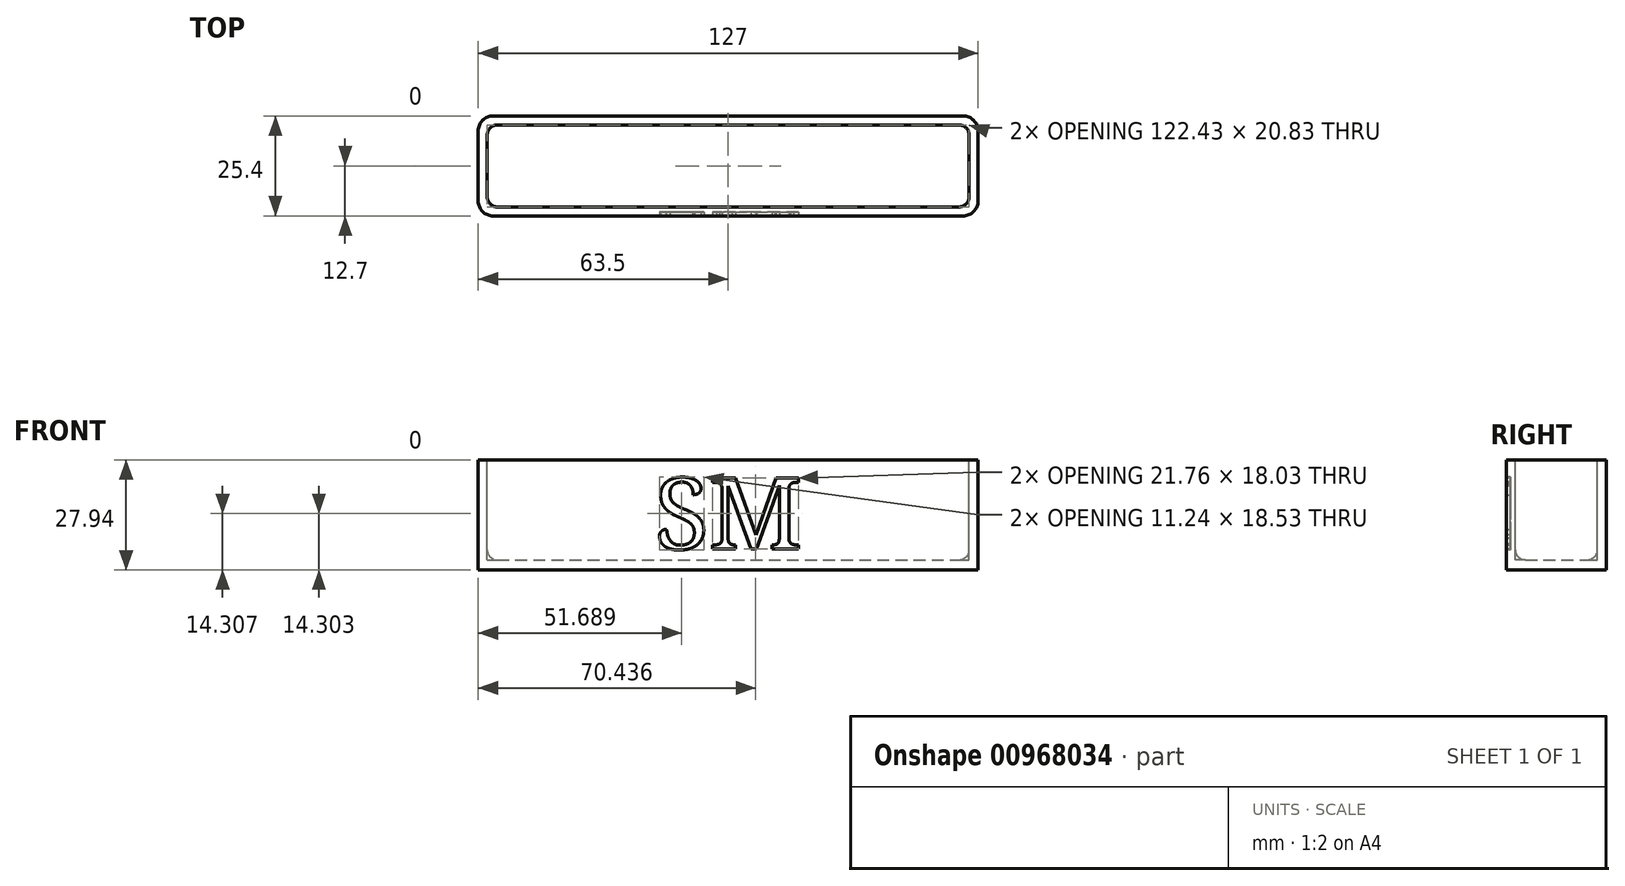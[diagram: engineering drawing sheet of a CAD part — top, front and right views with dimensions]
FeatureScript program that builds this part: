
annotation { "Feature Type Name" : "Feature", "Feature Type Description" : "" }
export const myFeature = defineFeature(function(context is Context, id is Id, definition is map)
    precondition{}
    {
        {
            var Q0;
            Q0=qCreatedBy(makeId("Top.planeOp"),FACE);
            var sketch = newSketch(context, id + "F0", { "sketchPlane" : qUnion([Q0])});
            skLineSegment(sketch, "E0.bottom", {"start": v(63.5, -12.7) * mm, "end": v(-63.5, -12.7) * mm});
            skLineSegment(sketch, "E0.top", {"start": v(63.5, 12.7) * mm, "end": v(-63.5, 12.7) * mm});
            skLineSegment(sketch, "E0.left", {"start": v(63.5, -12.7) * mm, "end": v(63.5, 12.7) * mm});
            skLineSegment(sketch, "E0.right", {"start": v(-63.5, -12.7) * mm, "end": v(-63.5, 12.7) * mm});
            skPoint(sketch, "E0.middle", {"position": v(0, 0) * mm});
            skSolve(sketch);
        }
        {
            var Q0;
            Q0=makeQuery(id+"F0.imprint","IMPRINT",FACE,{"disambiguationData":[TD([[makeQuery(id+"F0.imprint","IMPRINT",EDGE,{"derivedFrom":sQuery(id+"F0.wireOp",EDGE,"E0.bottom")}),-1.0]])]});
            extrude(context, id + "F1", {"entities" : qUnion([Q0]), "depth" : 27.94 * mm, "offsetDistance" : 25.4 * mm});
        }
        {
            var Q0;
            Q0=makeQuery(id+"F1.opExtrude","CAP_FACE",FACE,{"disambiguationData":[OSD([sQuery(id+"F0.wireOp",EDGE,"E0.bottom"),sQuery(id+"F0.wireOp",EDGE,"E0.top"),sQuery(id+"F0.wireOp",EDGE,"E0.left"),sQuery(id+"F0.wireOp",EDGE,"E0.right")])],"isStart":false});
            var sketch = newSketch(context, id + "F2", { "sketchPlane" : qUnion([Q0])});
            skLineSegment(sketch, "E1.0", {"start": v(61.21, -10.41) * mm, "end": v(61.21, 10.41) * mm});
            skLineSegment(sketch, "E1.1", {"start": v(-61.21, -10.41) * mm, "end": v(61.21, -10.41) * mm});
            skLineSegment(sketch, "E1.2", {"start": v(-61.21, 10.41) * mm, "end": v(-61.21, -10.41) * mm});
            skLineSegment(sketch, "E1.3", {"start": v(61.21, 10.41) * mm, "end": v(-61.21, 10.41) * mm});
            skSolve(sketch);
        }
        {
            var Q0;
            Q0=makeQuery(id+"F2.imprint","IMPRINT",FACE,{"disambiguationData":[TD([[makeQuery(id+"F2.imprint","IMPRINT",EDGE,{"derivedFrom":sQuery(id+"F2.wireOp",EDGE,"E1.0")}),1.0]])]});
            extrude(context, id + "F3", {"entities" : qUnion([Q0]), "operationType" : NewBodyOperationType.REMOVE, "oppositeDirection" : true, "depth" : 25.4 * mm, "offsetDistance" : 25.4 * mm});
        }
        {
            var Q0;
            Q0=makeQuery(id+"F3.boolean.opBoolean","COPY",FACE,{"derivedFrom":makeQuery(id+"F3.opExtrude","CAP_FACE",FACE,{"disambiguationData":[OSD([sQuery(id+"F2.wireOp",EDGE,"E1.0"),sQuery(id+"F2.wireOp",EDGE,"E1.1"),sQuery(id+"F2.wireOp",EDGE,"E1.2"),sQuery(id+"F2.wireOp",EDGE,"E1.3")])],"isStart":false})});
            var Q1;
            Q1=makeQuery(id+"F3.boolean.opBoolean","COPY",EDGE,{"derivedFrom":makeQuery(id+"F3.opExtrude","SWEPT_EDGE",EDGE,{"disambiguationData":[OSD([sQuery(id+"F2.wireOp",EDGE,"E1.2"),sQuery(id+"F2.wireOp",EDGE,"E1.3")])]})});
            var Q2;
            Q2=makeQuery(id+"F3.boolean.opBoolean","COPY",EDGE,{"derivedFrom":makeQuery(id+"F3.opExtrude","SWEPT_EDGE",EDGE,{"disambiguationData":[OSD([sQuery(id+"F2.wireOp",EDGE,"E1.0"),sQuery(id+"F2.wireOp",EDGE,"E1.3")])]})});
            var Q3;
            Q3=makeQuery(id+"F3.boolean.opBoolean","COPY",EDGE,{"derivedFrom":makeQuery(id+"F3.opExtrude","SWEPT_EDGE",EDGE,{"disambiguationData":[OSD([sQuery(id+"F2.wireOp",EDGE,"E1.0"),sQuery(id+"F2.wireOp",EDGE,"E1.1")])]})});
            var Q4;
            Q4=makeQuery(id+"F3.boolean.opBoolean","COPY",EDGE,{"derivedFrom":makeQuery(id+"F3.opExtrude","SWEPT_EDGE",EDGE,{"disambiguationData":[OSD([sQuery(id+"F2.wireOp",EDGE,"E1.1"),sQuery(id+"F2.wireOp",EDGE,"E1.2")])]})});
            fillet(context, id + "F4", {"entities" : qUnion([Q0, Q1, Q2, Q3, Q4]), "radius" : 2.54 * mm, "tangentPropagation" : true, "allowEdgeOverflow" : false});
        }
        {
            var Q0;
            Q0=makeQuery(id+"F1.opExtrude","SWEPT_EDGE",EDGE,{"disambiguationData":[OSD([sQuery(id+"F0.wireOp",EDGE,"E0.bottom"),sQuery(id+"F0.wireOp",EDGE,"E0.right")])]});
            var Q1;
            Q1=makeQuery(id+"F1.opExtrude","SWEPT_EDGE",EDGE,{"disambiguationData":[OSD([sQuery(id+"F0.wireOp",EDGE,"E0.top"),sQuery(id+"F0.wireOp",EDGE,"E0.right")])]});
            var Q2;
            Q2=makeQuery(id+"F1.opExtrude","SWEPT_EDGE",EDGE,{"disambiguationData":[OSD([sQuery(id+"F0.wireOp",EDGE,"E0.top"),sQuery(id+"F0.wireOp",EDGE,"E0.left")])]});
            var Q3;
            Q3=makeQuery(id+"F1.opExtrude","SWEPT_EDGE",EDGE,{"disambiguationData":[OSD([sQuery(id+"F0.wireOp",EDGE,"E0.bottom"),sQuery(id+"F0.wireOp",EDGE,"E0.left")])]});
            fillet(context, id + "F5", {"entities" : qUnion([Q0, Q1, Q2, Q3]), "radius" : 3.8 * mm, "tangentPropagation" : true, "allowEdgeOverflow" : false});
        }
        {
            var Q0;
            Q0=makeQuery(id+"F1.opExtrude","SWEPT_FACE",FACE,{"disambiguationData":[OSD([sQuery(id+"F0.wireOp",EDGE,"E0.bottom")])]});
            var sketch = newSketch(context, id + "F6", { "sketchPlane" : qUnion([Q0])});
            skLineSegment(sketch, "E2", {"start": v(0, 27.94) * mm, "end": v(0, 0) * mm, "construction": true});
            skText(sketch, "E3", { "text": "SM", "fontName": "NotoSerif-Regular.ttf"});
            const initialGuessF6  = {"E3": [-0.01864, 0.00529, 1, 0, 0.01818]};
            skSetInitialGuess(sketch, initialGuessF6);
            skSolve(sketch);
        }
        {
            var Q0;
            Q0 = qSketchRegion(id + "F6", true);
            extrude(context, id + "F7", {"entities" : qUnion([Q0]), "operationType" : NewBodyOperationType.REMOVE, "oppositeDirection" : true, "depth" : 1.02 * mm, "offsetDistance" : 25.4 * mm});
        }
    });
